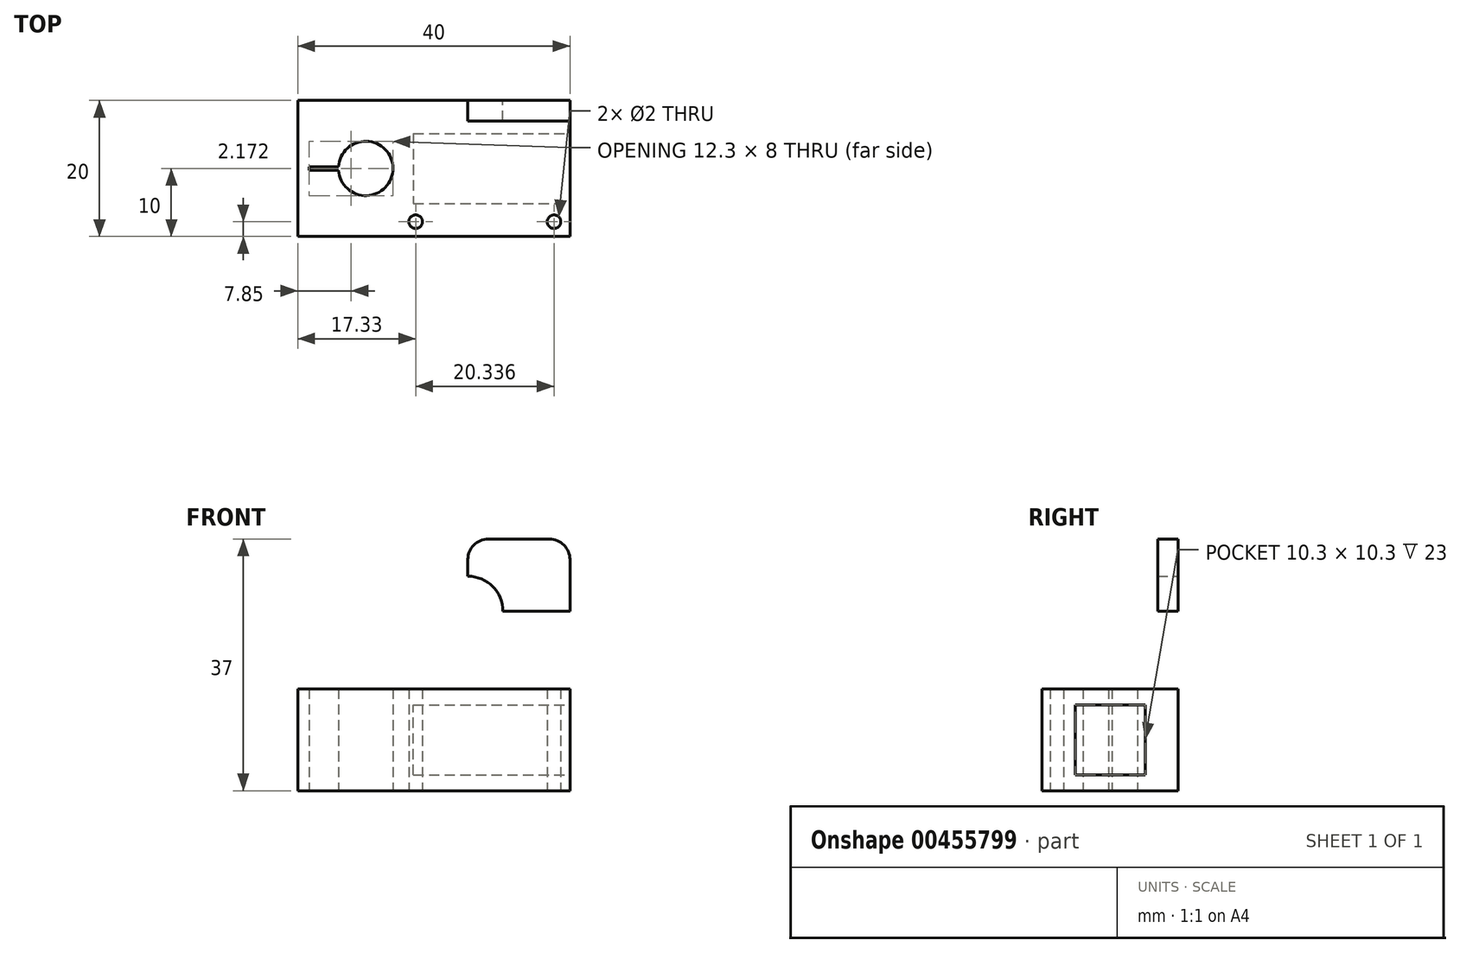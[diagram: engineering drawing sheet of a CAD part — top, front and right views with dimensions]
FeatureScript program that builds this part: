
annotation { "Feature Type Name" : "Feature", "Feature Type Description" : "" }
export const myFeature = defineFeature(function(context is Context, id is Id, definition is map)
    precondition{}
    {
        {
            var Q0;
            Q0=qCreatedBy(makeId("Top.planeOp"),FACE);
            var sketch = newSketch(context, id + "F0", { "sketchPlane" : qUnion([Q0])});
            skCircle(sketch, "E0", {"center": v(0, 0) * mm, "radius": 4 * mm});
            skLineSegment(sketch, "E1.bottom", {"start": v(-10, -10) * mm, "end": v(10, -10) * mm});
            skLineSegment(sketch, "E1.top", {"start": v(-10, 10) * mm, "end": v(10, 10) * mm});
            skLineSegment(sketch, "E1.left", {"start": v(-10, -10) * mm, "end": v(-10, 10) * mm});
            skLineSegment(sketch, "E1.right", {"start": v(10, -10) * mm, "end": v(10, 10) * mm});
            skLineSegment(sketch, "E2.bottom", {"start": v(10, 10) * mm, "end": v(30, 10) * mm});
            skLineSegment(sketch, "E2.top", {"start": v(10, -10) * mm, "end": v(30, -10) * mm});
            skLineSegment(sketch, "E2.left", {"start": v(10, 10) * mm, "end": v(10, -10) * mm});
            skLineSegment(sketch, "E2.right", {"start": v(30, 10) * mm, "end": v(30, -10) * mm});
            skPoint(sketch, "E3", {"position": v(-4, 0) * mm});
            skLineSegment(sketch, "E4.bottom", {"start": v(0, 0) * mm, "end": v(-8.3, 0) * mm});
            skLineSegment(sketch, "E4.top", {"start": v(0, 0.25) * mm, "end": v(-8.3, 0.25) * mm});
            skLineSegment(sketch, "E4.left", {"start": v(0, 0) * mm, "end": v(0, 0.25) * mm});
            skLineSegment(sketch, "E4.right", {"start": v(-8.3, 0) * mm, "end": v(-8.3, 0.25) * mm});
            skLineSegment(sketch, "E5.MirrorCS", {"start": v(0, -0.25) * mm, "end": v(-8.3, -0.25) * mm});
            skLineSegment(sketch, "E6.MirrorCS", {"start": v(-8.3, 0) * mm, "end": v(-8.3, -0.25) * mm});
            skLineSegment(sketch, "E7.MirrorCS", {"start": v(0, 0) * mm, "end": v(0, -0.25) * mm});
            skCircle(sketch, "E8", {"center": v(7.33, 7.83) * mm, "radius": 1 * mm});
            skCircle(sketch, "E9.MirrorC", {"center": v(7.33, -7.83) * mm, "radius": 1 * mm});
            skLineSegment(sketch, "E10", {"start": v(7.33, 7.83) * mm, "end": v(27.67, 7.83) * mm});
            skCircle(sketch, "E11", {"center": v(27.67, 7.83) * mm, "radius": 1 * mm});
            skCircle(sketch, "E12.MirrorC", {"center": v(27.67, -7.83) * mm, "radius": 1 * mm});
            skSolve(sketch);
        }
        {
            var Q0;
            {var subQ5=sQuery(id+"F0.wireOp",EDGE,"E1.bottom");Q0=makeQuery(id+"F0.imprint","IMPRINT",FACE,{"disambiguationData":[TD([[makeQuery(id+"F0.imprint","IMPRINT",EDGE,{"derivedFrom":subQ5}),1.0]])]});}
            var Q1;
            {var subQ3=sQuery(id+"F0.wireOp",EDGE,"E2.bottom");Q1=makeQuery(id+"F0.imprint","IMPRINT",FACE,{"disambiguationData":[TD([[makeQuery(id+"F0.imprint","IMPRINT",EDGE,{"derivedFrom":subQ3}),-1.0]])]});}
            var Q2;
            Q2=makeQuery(id+"F0.imprint","IMPRINT",FACE,{"disambiguationData":[TD([[makeQuery(id+"F0.imprint","IMPRINT",EDGE,{"derivedFrom":sQuery(id+"F0.wireOp",EDGE,"E8")}),1.0]])]});
            var Q3;
            Q3=makeQuery(id+"F0.imprint","IMPRINT",FACE,{"disambiguationData":[TD([[makeQuery(id+"F0.imprint","IMPRINT",EDGE,{"derivedFrom":sQuery(id+"F0.wireOp",EDGE,"E11")}),1.0]])]});
            extrude(context, id + "F1", {"entities" : qUnion([Q0, Q1, Q2, Q3]), "depth" : 15 * mm});
        }
        {
            var Q0;
            Q0=makeQuery(id+"F1.opExtrude","SWEPT_FACE",FACE,{"disambiguationData":[OSD([sQuery(id+"F0.wireOp",EDGE,"E2.right")])]});
            var sketch = newSketch(context, id + "F2", { "sketchPlane" : qUnion([Q0])});
            skPoint(sketch, "E13", {"position": v(-10, 7.5) * mm});
            skLineSegment(sketch, "E14", {"start": v(0, 7.5) * mm, "end": v(-10, 7.5) * mm});
            skLineSegment(sketch, "E15.bottom", {"start": v(5.15, 2.35) * mm, "end": v(-5.15, 2.35) * mm});
            skLineSegment(sketch, "E15.top", {"start": v(5.15, 12.65) * mm, "end": v(-5.15, 12.65) * mm});
            skLineSegment(sketch, "E15.left", {"start": v(5.15, 2.35) * mm, "end": v(5.15, 12.65) * mm});
            skLineSegment(sketch, "E15.right", {"start": v(-5.15, 2.35) * mm, "end": v(-5.15, 12.65) * mm});
            skPoint(sketch, "E15.middle", {"position": v(0, 7.5) * mm});
            skSolve(sketch);
        }
        {
            var Q0;
            {var subQ1=sQuery(id+"F2.wireOp",EDGE,"E15.bottom");Q0=makeQuery(id+"F2.imprint","IMPRINT",FACE,{"disambiguationData":[TD([[makeQuery(id+"F2.imprint","IMPRINT",EDGE,{"derivedFrom":subQ1}),-1.0]])]});}
            extrude(context, id + "F3", {"entities" : qUnion([Q0]), "operationType" : NewBodyOperationType.REMOVE, "oppositeDirection" : true, "depth" : 23 * mm});
        }
        {
            var Q0;
            Q0=makeQuery(id+"F1.opExtrude","SWEPT_FACE",FACE,{"disambiguationData":[OSD([sQuery(id+"F0.wireOp",EDGE,"E1.top"),sQuery(id+"F0.wireOp",EDGE,"E2.bottom")])]});
            var sketch = newSketch(context, id + "F4", { "sketchPlane" : qUnion([Q0])});
            skLineSegment(sketch, "E16.bottom", {"start": v(-30, 0) * mm, "end": v(0, 0) * mm});
            skLineSegment(sketch, "E16.top", {"start": v(-30, 37) * mm, "end": v(0, 37) * mm});
            skLineSegment(sketch, "E16.left", {"start": v(-30, 0) * mm, "end": v(-30, 37) * mm});
            skLineSegment(sketch, "E16.right", {"start": v(0, 0) * mm, "end": v(0, 37) * mm});
            skLineSegment(sketch, "E17.bottom", {"start": v(-30, 37) * mm, "end": v(-15, 37) * mm});
            skLineSegment(sketch, "E17.top", {"start": v(-30, 26.4) * mm, "end": v(-15, 26.4) * mm});
            skLineSegment(sketch, "E17.left", {"start": v(-30, 37) * mm, "end": v(-30, 26.4) * mm});
            skLineSegment(sketch, "E17.right", {"start": v(-15, 37) * mm, "end": v(-15, 26.4) * mm});
            skCircle(sketch, "E18", {"center": v(-15, 26.4) * mm, "radius": 5.15 * mm});
            skSolve(sketch);
        }
        {
            var Q0;
            {var subQ1=sQuery(id+"F4.wireOp",EDGE,"E17.bottom");Q0=makeQuery(id+"F4.imprint","IMPRINT",FACE,{"disambiguationData":[TD([[makeQuery(id+"F4.imprint","IMPRINT",EDGE,{"derivedFrom":subQ1}),-1.0]])]});}
            var Q1;
            {var subQ0=sQuery(id+"F4.wireOp",EDGE,"E16.bottom");Q1=makeQuery(id+"F4.imprint","IMPRINT",FACE,{"disambiguationData":[TD([[makeQuery(id+"F4.imprint","IMPRINT",EDGE,{"derivedFrom":subQ0}),-1.0]])]});}
            var Q2;
            {var subQ6=sQuery(id+"F4.wireOp",EDGE,"E16.top");Q2=makeQuery(id+"F4.imprint","IMPRINT",FACE,{"disambiguationData":[TD([[makeQuery(id+"F4.imprint","IMPRINT",EDGE,{"derivedFrom":subQ6}),-1.0]])]});}
            extrude(context, id + "F5", {"entities" : qUnion([Q0, Q1, Q2]), "operationType" : NewBodyOperationType.ADD, "oppositeDirection" : true, "depth" : 3 * mm});
        }
        {
            var Q0;
            Q0=makeQuery(id+"F5.opExtrude","SWEPT_EDGE",EDGE,{"disambiguationData":[OSD([sQuery(id+"F4.wireOp",EDGE,"E17.bottom"),sQuery(id+"F4.wireOp",EDGE,"E17.left")])]});
            var Q1;
            Q1=makeQuery(id+"F5.opExtrude","SWEPT_EDGE",EDGE,{"disambiguationData":[OSD([sQuery(id+"F4.wireOp",EDGE,"E16.top"),sQuery(id+"F4.wireOp",EDGE,"E16.right")])]});
            fillet(context, id + "F6", {"entities" : qUnion([Q0, Q1]), "radius" : 3 * mm, "tangentPropagation" : true, "allowEdgeOverflow" : false});
        }
    });
